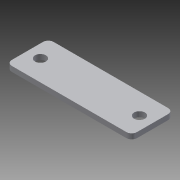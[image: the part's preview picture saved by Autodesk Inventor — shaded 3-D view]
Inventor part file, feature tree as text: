
AUTODESK INVENTOR PART (.ipt)
format: ipt  version: 2014 SP1 (Build 180222100, 222)  size: 87,040 bytes
history: native  units: in
note: dims shown in document units (in); Inventor stores cm internally (conversion verified against a paired STEP export)
features: extrude x1, fillet x1, sketch x1
ambient origin geometry x8: Origin, YZ Plane, XZ Plane, XY Plane, X Axis, Y Axis, Z Axis, Center Point
bodies: Solid1 (feature_tree)
feature tree (3):
  extrude  "Extrusion1"  Depth=0.125in
  fillet  "Fillet1"  Radius=2.375in
  sketch  "Sketch1"  dims[d0=3.0in d1=0.26in d2=2.375in d3=1.0in d4=0.125in d5=0.0in d6=0.125in]
